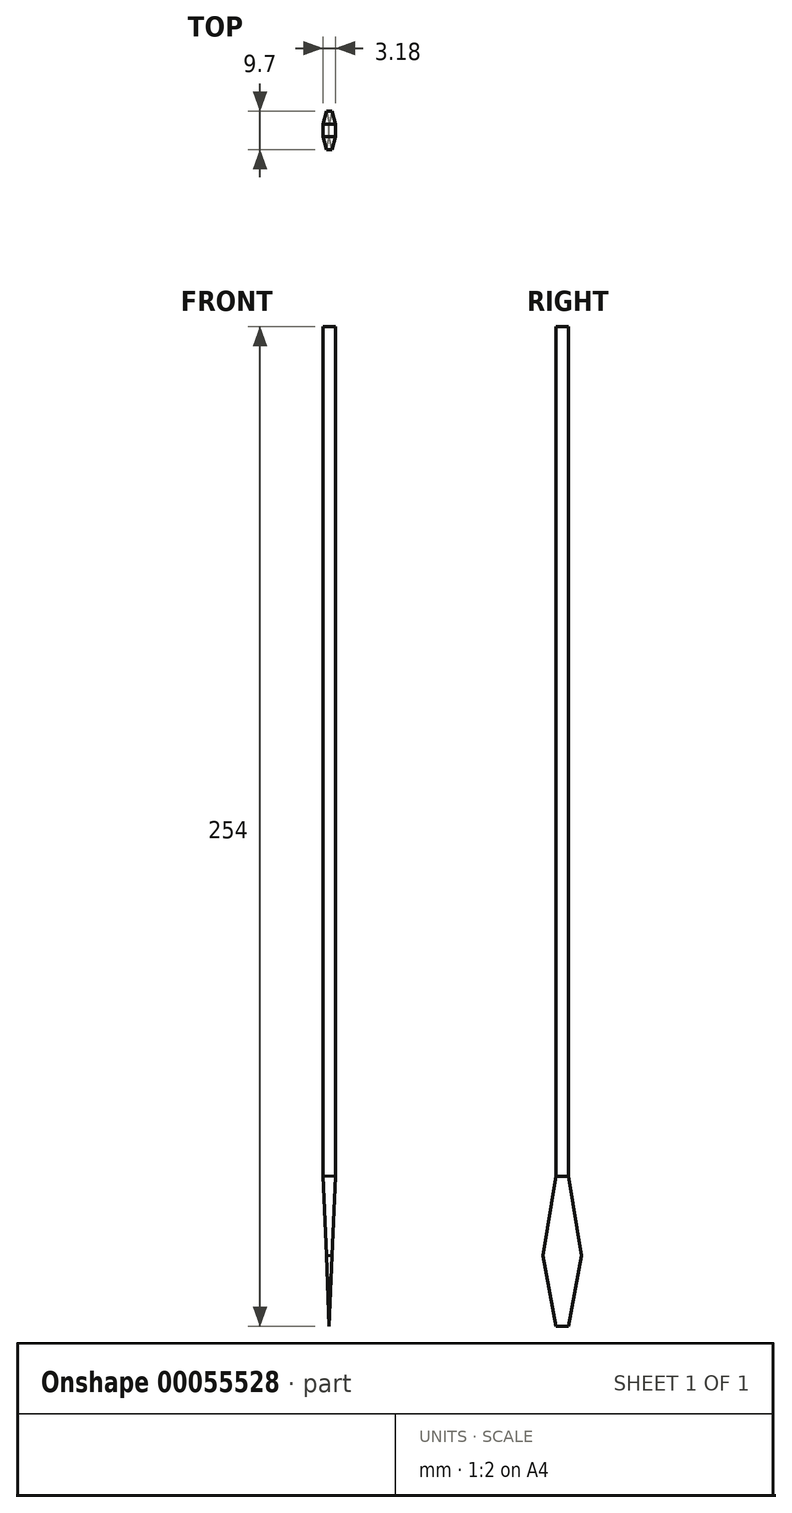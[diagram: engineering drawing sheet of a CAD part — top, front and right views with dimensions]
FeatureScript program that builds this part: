
annotation { "Feature Type Name" : "Feature", "Feature Type Description" : "" }
export const myFeature = defineFeature(function(context is Context, id is Id, definition is map)
    precondition{}
    {
        {
            var Q0;
            Q0=qCreatedBy(makeId("Front.planeOp"),FACE);
            var sketch = newSketch(context, id + "F0", { "sketchPlane" : qUnion([Q0])});
            skLineSegment(sketch, "E0.bottom", {"start": v(-47.9, 231.93) * mm, "end": v(-44.73, 231.93) * mm});
            skLineSegment(sketch, "E0.left", {"start": v(-47.9, 231.93) * mm, "end": v(-47.9, 16.03) * mm});
            skLineSegment(sketch, "E0.right", {"start": v(-44.73, 231.93) * mm, "end": v(-44.73, 16.03) * mm});
            skLineSegment(sketch, "E1.0", {"start": v(-47.9, 16.03) * mm, "end": v(-44.73, 16.03) * mm, "construction": true});
            skLineSegment(sketch, "E2", {"start": v(-44.73, 16.03) * mm, "end": v(-46.32, -22.07) * mm});
            skLineSegment(sketch, "E3", {"start": v(-46.32, -22.07) * mm, "end": v(-47.9, 16.03) * mm});
            skPoint(sketch, "E4.orphan", {"position": v(-44.73, -22.07) * mm});
            skPoint(sketch, "E0.top.start.orphan", {"position": v(-47.9, -22.07) * mm});
            skSolve(sketch);
        }
        {
            var Q0;
            Q0 = qSketchRegion(id + "F0", true);
            extrude(context, id + "F1", {"entities" : qUnion([Q0]), "depth" : 3.17 * mm});
        }
        {
            var Q0;
            Q0=makeQuery(id+"F1.opExtrude","SWEPT_FACE",FACE,{"disambiguationData":[OSD([sQuery(id+"F0.wireOp",EDGE,"E2")])]});
            var sketch = newSketch(context, id + "F2", { "sketchPlane" : qUnion([Q0])});
            skLineSegment(sketch, "E5", {"start": v(0, 14.15) * mm, "end": v(3.26, -6.06) * mm});
            skLineSegment(sketch, "E6", {"start": v(3.26, -6.06) * mm, "end": v(0, -23.98) * mm});
            skLineSegment(sketch, "E7.0", {"start": v(-1.59, 14.15) * mm, "end": v(-1.59, -23.98) * mm, "construction": true});
            skLineSegment(sketch, "E8.MirrorCS", {"start": v(-6.44, -6.06) * mm, "end": v(-3.17, -23.98) * mm});
            skLineSegment(sketch, "E9.MirrorCS", {"start": v(-3.17, 14.15) * mm, "end": v(-6.44, -6.06) * mm});
            skSolve(sketch);
        }
        {
            var Q0;
            Q0 = qSketchRegion(id + "F2", true);
            var Q1;
            Q1=makeQuery(id+"F2.imprint","IMPRINT",FACE,{"disambiguationData":[TD([[makeQuery(id+"F2.imprint","IMPRINT",EDGE,{"derivedFrom":sQuery(id+"F2.wireOp",EDGE,"E8.MirrorCS")}),1.0]])]});
            var Q2;
            Q2=makeQuery(id+"F2.imprint","IMPRINT",FACE,{"disambiguationData":[TD([[makeQuery(id+"F2.imprint","IMPRINT",EDGE,{"derivedFrom":sQuery(id+"F2.wireOp",EDGE,"E5")}),-1.0]])]});
            var Q3;
            Q3=makeQuery(id+"F1.opExtrude","SWEPT_FACE",FACE,{"disambiguationData":[OSD([sQuery(id+"F0.wireOp",EDGE,"E3")])]});
            extrude(context, id + "F3", {"entities" : qUnion([Q0, Q1, Q2]), "operationType" : NewBodyOperationType.ADD, "endBound" : BoundingType.UP_TO_SURFACE, "oppositeDirection" : true, "endBoundEntityFace" : qUnion([Q3]), "depth" : 25.4 * mm});
        }
    });
